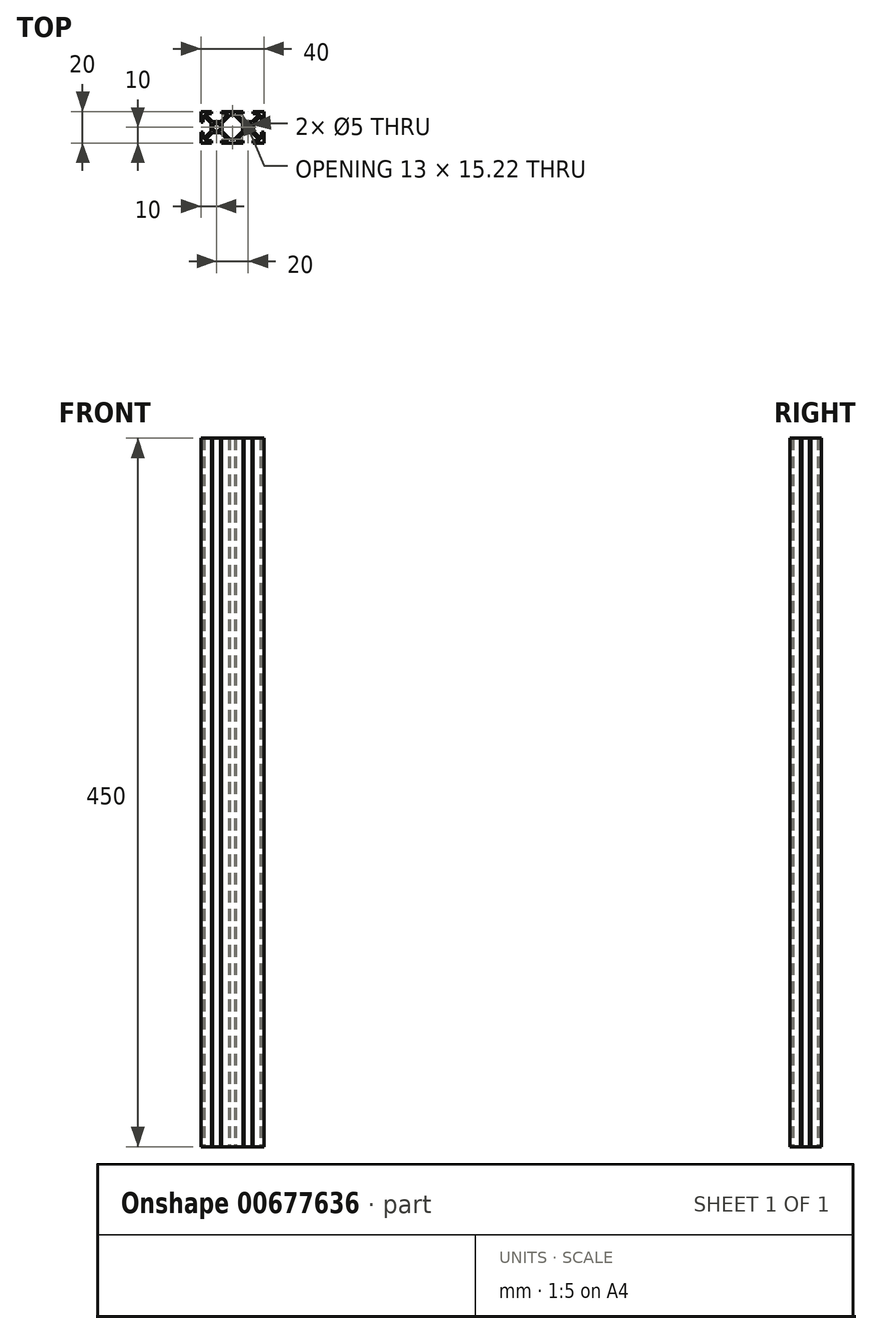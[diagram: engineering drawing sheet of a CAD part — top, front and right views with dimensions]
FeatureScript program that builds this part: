
annotation { "Feature Type Name" : "Feature", "Feature Type Description" : "" }
export const myFeature = defineFeature(function(context is Context, id is Id, definition is map)
    precondition{}
    {
        {
            var Q0;
            Q0=qCreatedBy(makeId("Top.planeOp"),FACE);
            var sketch = newSketch(context, id + "F0", { "sketchPlane" : qUnion([Q0])});
            skCircle(sketch, "E0", {"center": v(10, 10) * mm, "radius": 2.5 * mm});
            skLineSegment(sketch, "E1", {"start": v(0, 0) * mm, "end": v(10, 10) * mm, "construction": true});
            skLineSegment(sketch, "E2", {"start": v(1.4, 2.39) * mm, "end": v(1.4, 6.8) * mm});
            skLineSegment(sketch, "E3", {"start": v(1.4, 6.8) * mm, "end": v(0, 6.8) * mm});
            skLineSegment(sketch, "E4", {"start": v(0, 6.8) * mm, "end": v(0, 0) * mm});
            skLineSegment(sketch, "E5", {"start": v(7.49, 6.5) * mm, "end": v(2.39, 1.4) * mm});
            skLineSegment(sketch, "E6", {"start": v(2.39, 1.4) * mm, "end": v(6.8, 1.4) * mm});
            skLineSegment(sketch, "E7", {"start": v(6.8, 1.4) * mm, "end": v(6.8, 0) * mm});
            skLineSegment(sketch, "E8", {"start": v(6.8, 0) * mm, "end": v(0, 0) * mm});
            skLineSegment(sketch, "E9", {"start": v(10, 10) * mm, "end": v(20, 20) * mm, "construction": true});
            skLineSegment(sketch, "E10", {"start": v(10, 10) * mm, "end": v(0, 20) * mm, "construction": true});
            skLineSegment(sketch, "E11", {"start": v(10, 10) * mm, "end": v(20, 0) * mm, "construction": true});
            skLineSegment(sketch, "E12", {"start": v(1.4, 17.61) * mm, "end": v(6.5, 12.51) * mm});
            skLineSegment(sketch, "E13", {"start": v(1.4, 17.61) * mm, "end": v(1.4, 13.2) * mm});
            skLineSegment(sketch, "E14", {"start": v(1.4, 13.2) * mm, "end": v(0, 13.2) * mm});
            skLineSegment(sketch, "E15", {"start": v(0, 13.2) * mm, "end": v(0, 20) * mm});
            skLineSegment(sketch, "E16", {"start": v(7.49, 13.5) * mm, "end": v(2.39, 18.6) * mm});
            skLineSegment(sketch, "E17", {"start": v(2.39, 18.6) * mm, "end": v(6.8, 18.6) * mm});
            skLineSegment(sketch, "E18", {"start": v(6.8, 18.6) * mm, "end": v(6.8, 20) * mm});
            skLineSegment(sketch, "E19", {"start": v(6.8, 20) * mm, "end": v(0, 20) * mm});
            skLineSegment(sketch, "E20", {"start": v(12.51, 13.5) * mm, "end": v(17.61, 18.6) * mm});
            skLineSegment(sketch, "E21", {"start": v(17.61, 18.6) * mm, "end": v(13.2, 18.6) * mm});
            skLineSegment(sketch, "E22", {"start": v(13.2, 18.6) * mm, "end": v(13.2, 20) * mm});
            skLineSegment(sketch, "E23", {"start": v(13.2, 20) * mm, "end": v(20, 20) * mm});
            skLineSegment(sketch, "E24", {"start": v(13.5, 12.51) * mm, "end": v(18.6, 17.61) * mm});
            skLineSegment(sketch, "E25", {"start": v(12.51, 6.5) * mm, "end": v(17.61, 1.4) * mm});
            skLineSegment(sketch, "E26", {"start": v(17.61, 1.4) * mm, "end": v(13.2, 1.4) * mm});
            skLineSegment(sketch, "E27", {"start": v(13.2, 1.4) * mm, "end": v(13.2, 0) * mm});
            skLineSegment(sketch, "E28", {"start": v(13.2, 0) * mm, "end": v(20, 0) * mm});
            skLineSegment(sketch, "E29", {"start": v(12.51, 6.5) * mm, "end": v(7.49, 6.5) * mm});
            skLineSegment(sketch, "E30", {"start": v(7.49, 13.5) * mm, "end": v(12.51, 13.5) * mm});
            skLineSegment(sketch, "E31", {"start": v(10, 10) * mm, "end": v(10, 0) * mm, "construction": true});
            skLineSegment(sketch, "E32", {"start": v(10, 10) * mm, "end": v(18.77, 10) * mm, "construction": true});
            skLineSegment(sketch, "E33", {"start": v(10, 10) * mm, "end": v(10, 20.74) * mm, "construction": true});
            skLineSegment(sketch, "E34", {"start": v(10, 10) * mm, "end": v(0, 10) * mm, "construction": true});
            skLineSegment(sketch, "E35.bottom", {"start": v(0, 0) * mm, "end": v(20, 0) * mm, "construction": true});
            skLineSegment(sketch, "E35.top", {"start": v(0, 20) * mm, "end": v(20, 20) * mm, "construction": true});
            skLineSegment(sketch, "E35.left", {"start": v(0, 0) * mm, "end": v(0, 20) * mm, "construction": true});
            skLineSegment(sketch, "E36", {"start": v(18.6, 2.39) * mm, "end": v(13.5, 7.49) * mm});
            skLineSegment(sketch, "E37", {"start": v(13.5, 7.49) * mm, "end": v(13.5, 12.51) * mm});
            skLineSegment(sketch, "E38", {"start": v(1.4, 2.39) * mm, "end": v(6.5, 7.62) * mm});
            skLineSegment(sketch, "E39", {"start": v(6.5, 7.62) * mm, "end": v(6.5, 12.51) * mm});
            skCircle(sketch, "E40", {"center": v(30, 10) * mm, "radius": 2.5 * mm});
            skLineSegment(sketch, "E41", {"start": v(20, 0) * mm, "end": v(30, 10) * mm, "construction": true});
            skLineSegment(sketch, "E42", {"start": v(27.49, 6.5) * mm, "end": v(22.39, 1.4) * mm});
            skLineSegment(sketch, "E43", {"start": v(22.39, 1.4) * mm, "end": v(26.8, 1.4) * mm});
            skLineSegment(sketch, "E44", {"start": v(26.8, 1.4) * mm, "end": v(26.8, 0) * mm});
            skLineSegment(sketch, "E45", {"start": v(26.8, 0) * mm, "end": v(20, 0) * mm});
            skLineSegment(sketch, "E46", {"start": v(30, 10) * mm, "end": v(40, 20) * mm, "construction": true});
            skLineSegment(sketch, "E47", {"start": v(30, 10) * mm, "end": v(20, 20) * mm, "construction": true});
            skLineSegment(sketch, "E48", {"start": v(30, 10) * mm, "end": v(40, 0) * mm, "construction": true});
            skLineSegment(sketch, "E49", {"start": v(21.4, 17.61) * mm, "end": v(26.5, 12.51) * mm});
            skLineSegment(sketch, "E50", {"start": v(27.49, 13.5) * mm, "end": v(22.39, 18.6) * mm});
            skLineSegment(sketch, "E51", {"start": v(22.39, 18.6) * mm, "end": v(26.8, 18.6) * mm});
            skLineSegment(sketch, "E52", {"start": v(26.8, 18.6) * mm, "end": v(26.8, 20) * mm});
            skLineSegment(sketch, "E53", {"start": v(26.8, 20) * mm, "end": v(20, 20) * mm});
            skLineSegment(sketch, "E54", {"start": v(32.51, 13.5) * mm, "end": v(37.61, 18.6) * mm});
            skLineSegment(sketch, "E55", {"start": v(37.61, 18.6) * mm, "end": v(33.2, 18.6) * mm});
            skLineSegment(sketch, "E56", {"start": v(33.2, 18.6) * mm, "end": v(33.2, 20) * mm});
            skLineSegment(sketch, "E57", {"start": v(33.2, 20) * mm, "end": v(40, 20) * mm});
            skLineSegment(sketch, "E58", {"start": v(33.5, 12.51) * mm, "end": v(38.6, 17.61) * mm});
            skLineSegment(sketch, "E59", {"start": v(38.6, 17.61) * mm, "end": v(38.6, 13.2) * mm});
            skLineSegment(sketch, "E60", {"start": v(38.6, 13.2) * mm, "end": v(40, 13.2) * mm});
            skLineSegment(sketch, "E61", {"start": v(40, 13.2) * mm, "end": v(40, 20) * mm});
            skLineSegment(sketch, "E62", {"start": v(38.6, 2.39) * mm, "end": v(38.6, 6.8) * mm});
            skLineSegment(sketch, "E63", {"start": v(38.6, 6.8) * mm, "end": v(40, 6.8) * mm});
            skLineSegment(sketch, "E64", {"start": v(40, 6.8) * mm, "end": v(40, 0) * mm});
            skLineSegment(sketch, "E65", {"start": v(32.51, 6.5) * mm, "end": v(37.61, 1.4) * mm});
            skLineSegment(sketch, "E66", {"start": v(37.61, 1.4) * mm, "end": v(33.2, 1.4) * mm});
            skLineSegment(sketch, "E67", {"start": v(33.2, 1.4) * mm, "end": v(33.2, 0) * mm});
            skLineSegment(sketch, "E68", {"start": v(33.2, 0) * mm, "end": v(40, 0) * mm});
            skLineSegment(sketch, "E69", {"start": v(32.51, 6.5) * mm, "end": v(27.49, 6.5) * mm});
            skLineSegment(sketch, "E70", {"start": v(27.49, 13.5) * mm, "end": v(32.51, 13.5) * mm});
            skLineSegment(sketch, "E71", {"start": v(30, 10) * mm, "end": v(30, -4.28) * mm, "construction": true});
            skLineSegment(sketch, "E72", {"start": v(30, 10) * mm, "end": v(45.86, 10) * mm, "construction": true});
            skLineSegment(sketch, "E73", {"start": v(30, 10) * mm, "end": v(30, 16.47) * mm, "construction": true});
            skLineSegment(sketch, "E74", {"start": v(30, 10) * mm, "end": v(27.1, 10) * mm, "construction": true});
            skLineSegment(sketch, "E75.bottom", {"start": v(20, 0) * mm, "end": v(40, 0) * mm, "construction": true});
            skLineSegment(sketch, "E75.top", {"start": v(20, 20) * mm, "end": v(40, 20) * mm, "construction": true});
            skLineSegment(sketch, "E75.right", {"start": v(40, 0) * mm, "end": v(40, 20) * mm, "construction": true});
            skLineSegment(sketch, "E76", {"start": v(38.6, 2.39) * mm, "end": v(33.5, 7.49) * mm});
            skLineSegment(sketch, "E77", {"start": v(33.5, 7.49) * mm, "end": v(33.5, 12.51) * mm});
            skLineSegment(sketch, "E78", {"start": v(21.4, 2.39) * mm, "end": v(26.5, 7.62) * mm});
            skLineSegment(sketch, "E79", {"start": v(26.5, 7.62) * mm, "end": v(26.5, 12.51) * mm});
            skLineSegment(sketch, "E80", {"start": v(18.6, 17.61) * mm, "end": v(21.4, 17.61) * mm});
            skLineSegment(sketch, "E81", {"start": v(18.6, 2.39) * mm, "end": v(21.4, 2.39) * mm});
            skSolve(sketch);
        }
        {
            var Q0;
            Q0=makeQuery(id+"F0.imprint","IMPRINT",FACE,{"disambiguationData":[TD([[makeQuery(id+"F0.imprint","IMPRINT",EDGE,{"derivedFrom":sQuery(id+"F0.wireOp",EDGE,"E0")}),-1.0]])]});
            extrude(context, id + "F1", {"entities" : qUnion([Q0]), "depth" : 450 * mm, "offsetDistance" : 25 * mm});
        }
    });
